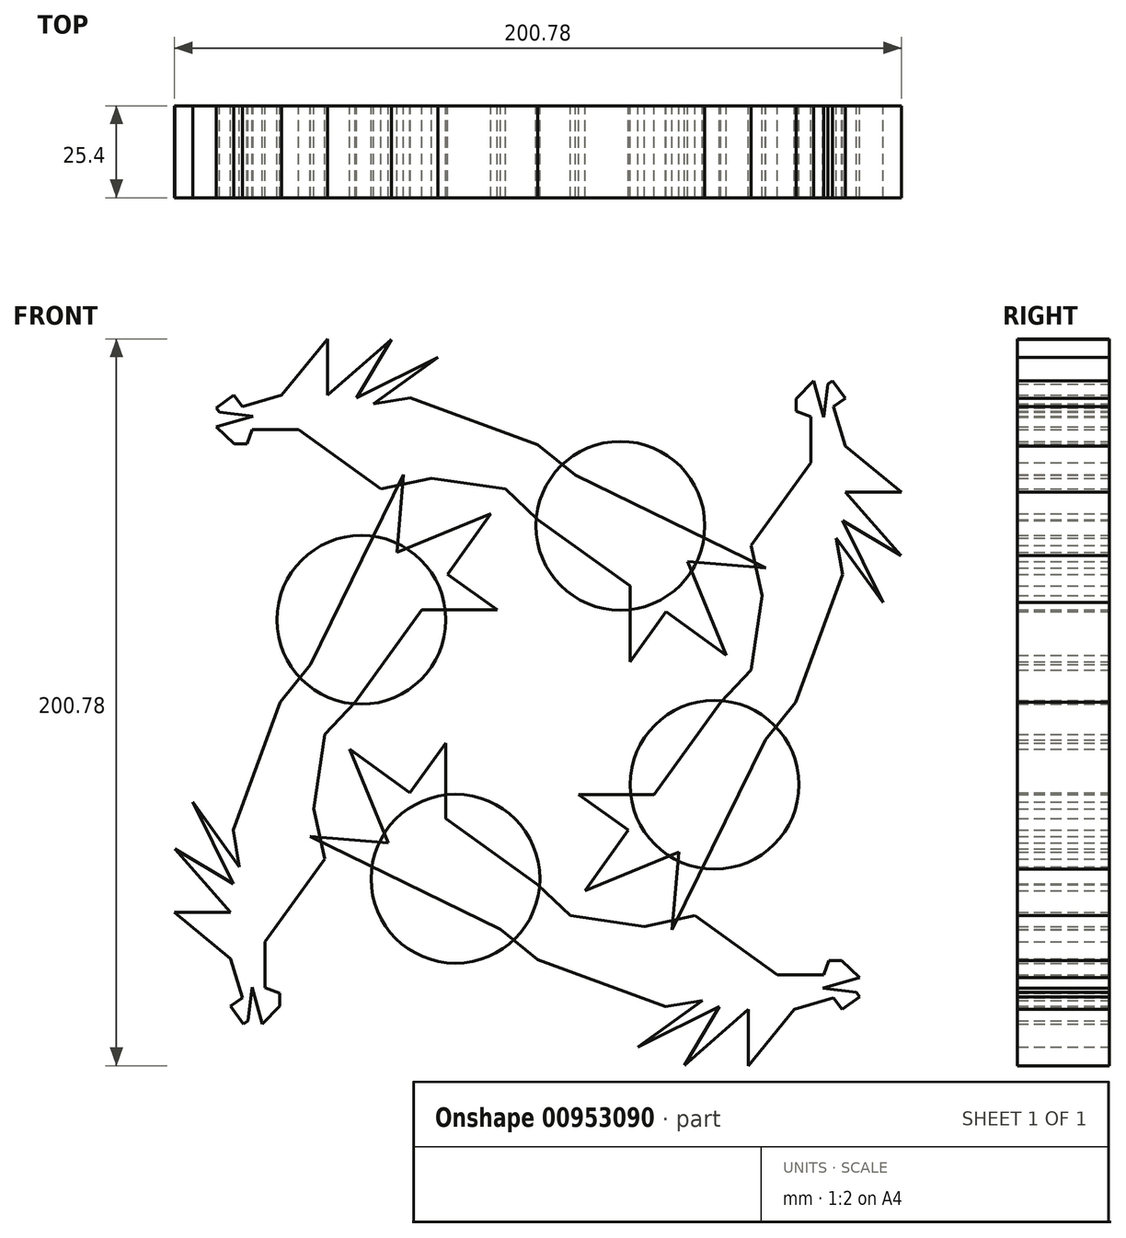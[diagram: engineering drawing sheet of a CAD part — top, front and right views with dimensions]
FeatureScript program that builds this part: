
annotation { "Feature Type Name" : "Feature", "Feature Type Description" : "" }
export const myFeature = defineFeature(function(context is Context, id is Id, definition is map)
    precondition{}
    {
        {
            var Q0;
            Q0=qCreatedBy(makeId("Front.planeOp"),FACE);
            var sketch = newSketch(context, id + "F0", { "sketchPlane" : qUnion([Q0])});
            skLineSegment(sketch, "E0", {"start": v(10.39, 62.75) * mm, "end": v(0, 71.16) * mm});
            skLineSegment(sketch, "E1", {"start": v(0, 71.16) * mm, "end": v(-35.28, 84.11) * mm});
            skLineSegment(sketch, "E2", {"start": v(-35.28, 84.11) * mm, "end": v(-45.39, 82.42) * mm});
            skLineSegment(sketch, "E3", {"start": v(-45.39, 82.42) * mm, "end": v(-27.6, 95.3) * mm});
            skLineSegment(sketch, "E4", {"start": v(-27.6, 95.3) * mm, "end": v(-50.16, 84.11) * mm});
            skLineSegment(sketch, "E5", {"start": v(-50.16, 84.11) * mm, "end": v(-40.47, 100.25) * mm});
            skLineSegment(sketch, "E6", {"start": v(-40.47, 100.25) * mm, "end": v(-58.06, 84.88) * mm});
            skLineSegment(sketch, "E7", {"start": v(-58.06, 84.88) * mm, "end": v(-58.06, 100.39) * mm});
            skLineSegment(sketch, "E8", {"start": v(-58.06, 100.39) * mm, "end": v(-70.8, 84.88) * mm});
            skLineSegment(sketch, "E9", {"start": v(-70.8, 84.88) * mm, "end": v(-81.62, 81.62) * mm});
            skLineSegment(sketch, "E10", {"start": v(-81.62, 81.62) * mm, "end": v(-83.98, 84.88) * mm});
            skLineSegment(sketch, "E11", {"start": v(-83.98, 84.88) * mm, "end": v(-88.83, 81.36) * mm});
            skLineSegment(sketch, "E12", {"start": v(-88.83, 81.36) * mm, "end": v(-87.93, 80.12) * mm});
            skLineSegment(sketch, "E13", {"start": v(-88.83, 76.1) * mm, "end": v(-83.88, 71.35) * mm});
            skLineSegment(sketch, "E14", {"start": v(-83.88, 71.35) * mm, "end": v(-80.37, 71.35) * mm});
            skLineSegment(sketch, "E15", {"start": v(-80.37, 71.35) * mm, "end": v(-78.9, 75.32) * mm});
            skLineSegment(sketch, "E16", {"start": v(-78.9, 75.32) * mm, "end": v(-66.15, 75.32) * mm});
            skLineSegment(sketch, "E17", {"start": v(-66.15, 75.32) * mm, "end": v(-43.32, 58.91) * mm});
            skLineSegment(sketch, "E18", {"start": v(-43.32, 58.91) * mm, "end": v(-29.44, 61.91) * mm});
            skLineSegment(sketch, "E19", {"start": v(-29.44, 61.91) * mm, "end": v(-8.9, 58.91) * mm});
            skLineSegment(sketch, "E20", {"start": v(0, 50.44) * mm, "end": v(-8.9, 58.91) * mm});
            skLineSegment(sketch, "E21", {"start": v(0, 50.44) * mm, "end": v(25.49, 32.13) * mm});
            skLineSegment(sketch, "E22", {"start": v(25.49, 32.13) * mm, "end": v(25.49, 11.25) * mm});
            skLineSegment(sketch, "E23", {"start": v(25.49, 11.25) * mm, "end": v(35.35, 24.98) * mm});
            skLineSegment(sketch, "E24", {"start": v(35.35, 24.98) * mm, "end": v(52.03, 13) * mm});
            skLineSegment(sketch, "E25", {"start": v(52.03, 13) * mm, "end": v(41.39, 38.88) * mm});
            skLineSegment(sketch, "E26", {"start": v(41.39, 38.88) * mm, "end": v(62.87, 37.08) * mm});
            skLineSegment(sketch, "E27", {"start": v(62.87, 37.08) * mm, "end": v(10.39, 62.75) * mm});
            skLineSegment(sketch, "E28", {"start": v(-87.93, 80.12) * mm, "end": v(-78.73, 79) * mm});
            skLineSegment(sketch, "E29", {"start": v(-78.73, 79) * mm, "end": v(-88.83, 76.1) * mm});
            skLineSegment(sketch, "E30.1.0", {"start": v(-61.63, -35.58) * mm, "end": v(-55.2, -72.6) * mm});
            skLineSegment(sketch, "E30.2.0", {"start": v(61.63, -35.58) * mm, "end": v(90.48, -11.5) * mm});
            skPoint(sketch, "E30.center", {"position": v(0, 0) * mm});
            skCircle(sketch, "E31", {"center": v(-22.78, -48.76) * mm, "radius": 23.31 * mm});
            skSolve(sketch);
        }
        {
            var Q0;
            Q0=qCreatedBy(makeId("Top.planeOp"),FACE);
            var sketch = newSketch(context, id + "F1", { "sketchPlane" : qUnion([Q0])});
            skLineSegment(sketch, "E32", {"start": v(0, 0) * mm, "end": v(0, -36.08) * mm});
            skSolve(sketch);
        }
        {
            var Q0;
            Q0 = qSketchRegion(id + "F0", true);
            extrude(context, id + "F2", {"entities" : qUnion([Q0]), "depth" : 25.4 * mm, "offsetDistance" : 25.4 * mm});
        }
        {
            var Q0;
            Q0=makeQuery(id+"F2.opExtrude","SWEPT_BODY",BODY,{"disambiguationData":[OSD([sQuery(id+"F0.wireOp",EDGE,"E0"),sQuery(id+"F0.wireOp",EDGE,"E1"),sQuery(id+"F0.wireOp",EDGE,"E2"),sQuery(id+"F0.wireOp",EDGE,"E3"),sQuery(id+"F0.wireOp",EDGE,"E4"),sQuery(id+"F0.wireOp",EDGE,"E5"),sQuery(id+"F0.wireOp",EDGE,"E6"),sQuery(id+"F0.wireOp",EDGE,"E7"),sQuery(id+"F0.wireOp",EDGE,"E8"),sQuery(id+"F0.wireOp",EDGE,"E9"),sQuery(id+"F0.wireOp",EDGE,"E10"),sQuery(id+"F0.wireOp",EDGE,"E11"),sQuery(id+"F0.wireOp",EDGE,"E12"),sQuery(id+"F0.wireOp",EDGE,"E13"),sQuery(id+"F0.wireOp",EDGE,"E14"),sQuery(id+"F0.wireOp",EDGE,"E15"),sQuery(id+"F0.wireOp",EDGE,"E16"),sQuery(id+"F0.wireOp",EDGE,"E17"),sQuery(id+"F0.wireOp",EDGE,"E18"),sQuery(id+"F0.wireOp",EDGE,"E19"),sQuery(id+"F0.wireOp",EDGE,"E20"),sQuery(id+"F0.wireOp",EDGE,"E21"),sQuery(id+"F0.wireOp",EDGE,"E22"),sQuery(id+"F0.wireOp",EDGE,"E23"),sQuery(id+"F0.wireOp",EDGE,"E24"),sQuery(id+"F0.wireOp",EDGE,"E25"),sQuery(id+"F0.wireOp",EDGE,"E26"),sQuery(id+"F0.wireOp",EDGE,"E27"),sQuery(id+"F0.wireOp",EDGE,"E28"),sQuery(id+"F0.wireOp",EDGE,"E29")])]});
            var Q1;
            Q1=makeQuery(id+"F2.opExtrude","SWEPT_BODY",BODY,{"disambiguationData":[OSD([sQuery(id+"F0.wireOp",EDGE,"E31")])]});
            var Q2;
            Q2=sQuery(id+"F1.wireOp",EDGE,"E32");
            circularPattern(context, id + "F3", {"entities" : qUnion([Q0, Q1]), "axis" : qUnion([Q2]), "angle" : 360 * degree, "instanceCount" : 4, "equalSpace" : true});
        }
    });
